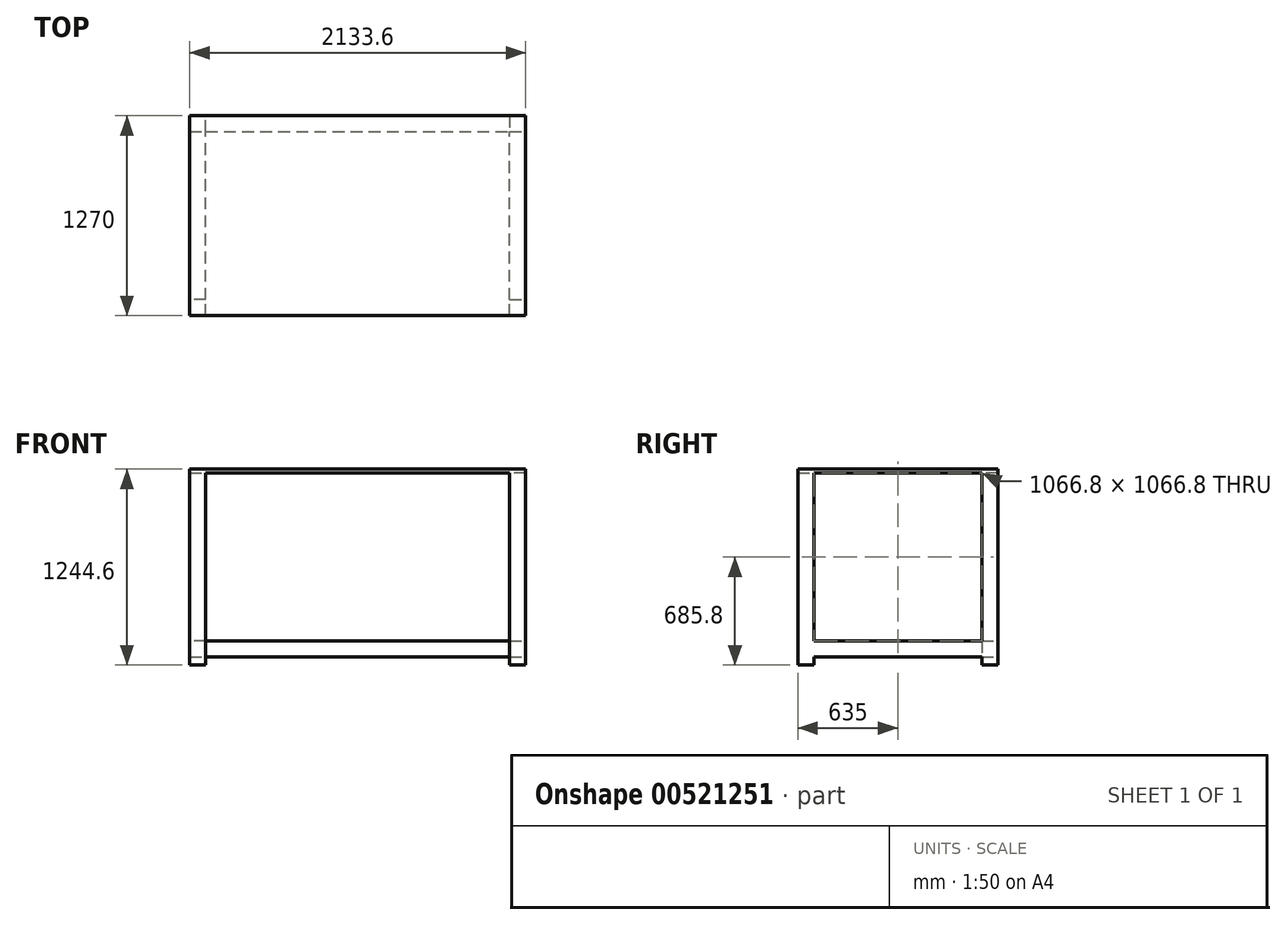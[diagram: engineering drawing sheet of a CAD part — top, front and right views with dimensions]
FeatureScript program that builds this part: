
annotation { "Feature Type Name" : "Feature", "Feature Type Description" : "" }
export const myFeature = defineFeature(function(context is Context, id is Id, definition is map)
    precondition{}
    {
        {
            var Q0;
            Q0=qCreatedBy(makeId("Top.planeOp"),FACE);
            var sketch = newSketch(context, id + "F0", { "sketchPlane" : qUnion([Q0])});
            skLineSegment(sketch, "E0.bottom", {"start": v(1066.8, -635) * mm, "end": v(-1066.8, -635) * mm, "construction": true});
            skLineSegment(sketch, "E0.top", {"start": v(1066.8, 635) * mm, "end": v(-1066.8, 635) * mm, "construction": true});
            skLineSegment(sketch, "E0.left", {"start": v(1066.8, -635) * mm, "end": v(1066.8, 635) * mm, "construction": true});
            skLineSegment(sketch, "E0.right", {"start": v(-1066.8, -635) * mm, "end": v(-1066.8, 635) * mm, "construction": true});
            skPoint(sketch, "E0.middle", {"position": v(0, 0) * mm});
            skLineSegment(sketch, "E1.bottom", {"start": v(-1066.8, 635) * mm, "end": v(-965.2, 635) * mm});
            skLineSegment(sketch, "E1.top", {"start": v(-1066.8, 533.4) * mm, "end": v(-965.2, 533.4) * mm});
            skLineSegment(sketch, "E1.left", {"start": v(-1066.8, 635) * mm, "end": v(-1066.8, 533.4) * mm});
            skLineSegment(sketch, "E1.right", {"start": v(-965.2, 635) * mm, "end": v(-965.2, 533.4) * mm});
            skLineSegment(sketch, "E2.bottom", {"start": v(-1066.8, -635) * mm, "end": v(-965.2, -635) * mm});
            skLineSegment(sketch, "E2.top", {"start": v(-1066.8, -533.4) * mm, "end": v(-965.2, -533.4) * mm});
            skLineSegment(sketch, "E2.left", {"start": v(-1066.8, -635) * mm, "end": v(-1066.8, -533.4) * mm});
            skLineSegment(sketch, "E2.right", {"start": v(-965.2, -635) * mm, "end": v(-965.2, -533.4) * mm});
            skLineSegment(sketch, "E3.bottom", {"start": v(1066.8, -635) * mm, "end": v(965.2, -635) * mm});
            skLineSegment(sketch, "E3.top", {"start": v(1066.8, -533.4) * mm, "end": v(965.2, -533.4) * mm});
            skLineSegment(sketch, "E3.left", {"start": v(1066.8, -635) * mm, "end": v(1066.8, -533.4) * mm});
            skLineSegment(sketch, "E3.right", {"start": v(965.2, -635) * mm, "end": v(965.2, -533.4) * mm});
            skLineSegment(sketch, "E4.bottom", {"start": v(1066.8, 635) * mm, "end": v(965.2, 635) * mm});
            skLineSegment(sketch, "E4.top", {"start": v(1066.8, 533.4) * mm, "end": v(965.2, 533.4) * mm});
            skLineSegment(sketch, "E4.left", {"start": v(1066.8, 635) * mm, "end": v(1066.8, 533.4) * mm});
            skLineSegment(sketch, "E4.right", {"start": v(965.2, 635) * mm, "end": v(965.2, 533.4) * mm});
            skSolve(sketch);
        }
        {
            var Q0;
            Q0 = qSketchRegion(id + "F0", true);
            extrude(context, id + "F1", {"entities" : qUnion([Q0]), "depth" : 1219.2 * mm, "offsetDistance" : 25.4 * mm});
        }
        {
            var Q0;
            Q0=makeQuery(id+"F1.opExtrude","CAP_FACE",FACE,{"disambiguationData":[OSD([sQuery(id+"F0.wireOp",EDGE,"E1.bottom"),sQuery(id+"F0.wireOp",EDGE,"E1.top"),sQuery(id+"F0.wireOp",EDGE,"E1.left"),sQuery(id+"F0.wireOp",EDGE,"E1.right")])],"isStart":false});
            var sketch = newSketch(context, id + "F2", { "sketchPlane" : qUnion([Q0])});
            skLineSegment(sketch, "E5.bottom", {"start": v(-1066.8, 635) * mm, "end": v(1066.8, 635) * mm});
            skLineSegment(sketch, "E5.top", {"start": v(-1066.8, -635) * mm, "end": v(1066.8, -635) * mm});
            skLineSegment(sketch, "E5.left", {"start": v(-1066.8, 635) * mm, "end": v(-1066.8, -635) * mm});
            skLineSegment(sketch, "E5.right", {"start": v(1066.8, 635) * mm, "end": v(1066.8, -635) * mm});
            skSolve(sketch);
        }
        {
            var Q0;
            Q0 = qSketchRegion(id + "F2", true);
            extrude(context, id + "F3", {"entities" : qUnion([Q0]), "operationType" : NewBodyOperationType.ADD, "depth" : 25.4 * mm, "offsetDistance" : 25.4 * mm});
        }
        {
            var Q0;
            Q0=makeQuery(id+"F1.opExtrude","SWEPT_FACE",FACE,{"disambiguationData":[OSD([sQuery(id+"F0.wireOp",EDGE,"E1.top")])]});
            var sketch = newSketch(context, id + "F4", { "sketchPlane" : qUnion([Q0])});
            skLineSegment(sketch, "E6", {"start": v(-1066.8, 0) * mm, "end": v(-1066.8, 50.8) * mm, "construction": true});
            skLineSegment(sketch, "E7.bottom", {"start": v(-1066.8, 50.8) * mm, "end": v(-965.2, 50.8) * mm});
            skLineSegment(sketch, "E7.top", {"start": v(-1066.8, 152.4) * mm, "end": v(-965.2, 152.4) * mm});
            skLineSegment(sketch, "E7.left", {"start": v(-1066.8, 50.8) * mm, "end": v(-1066.8, 152.4) * mm});
            skLineSegment(sketch, "E7.right", {"start": v(-965.2, 50.8) * mm, "end": v(-965.2, 152.4) * mm});
            skLineSegment(sketch, "E8.bottom", {"start": v(965.2, 50.8) * mm, "end": v(1066.8, 50.8) * mm});
            skLineSegment(sketch, "E8.top", {"start": v(965.2, 152.4) * mm, "end": v(1066.8, 152.4) * mm});
            skLineSegment(sketch, "E8.left", {"start": v(965.2, 50.8) * mm, "end": v(965.2, 152.4) * mm});
            skLineSegment(sketch, "E8.right", {"start": v(1066.8, 50.8) * mm, "end": v(1066.8, 152.4) * mm});
            skSolve(sketch);
        }
        {
            var Q0;
            Q0 = qSketchRegion(id + "F4", true);
            extrude(context, id + "F5", {"entities" : qUnion([Q0]), "operationType" : NewBodyOperationType.ADD, "endBound" : BoundingType.UP_TO_NEXT, "depth" : 25.4 * mm, "offsetDistance" : 25.4 * mm});
        }
        {
            var Q0;
            Q0=makeQuery(id+"F5.boolean.opBoolean","MERGE",FACE,{"derivedFrom":[makeQuery(id+"F1.opExtrude","SWEPT_FACE",FACE,{"disambiguationData":[OSD([sQuery(id+"F0.wireOp",EDGE,"E3.right")])]}),makeQuery(id+"F1.opExtrude","SWEPT_FACE",FACE,{"disambiguationData":[OSD([sQuery(id+"F0.wireOp",EDGE,"E4.right")])]}),makeQuery(id+"F5.opExtrude","SWEPT_FACE",FACE,{"disambiguationData":[OSD([sQuery(id+"F4.wireOp",EDGE,"E8.left")])]})]});
            var sketch = newSketch(context, id + "F6", { "sketchPlane" : qUnion([Q0])});
            skLineSegment(sketch, "E9", {"start": v(-635, 0) * mm, "end": v(-635, 50.8) * mm, "construction": true});
            skLineSegment(sketch, "E10.bottom", {"start": v(-635, 50.8) * mm, "end": v(-533.4, 50.8) * mm});
            skLineSegment(sketch, "E10.top", {"start": v(-635, 152.4) * mm, "end": v(-533.4, 152.4) * mm});
            skLineSegment(sketch, "E10.left", {"start": v(-635, 50.8) * mm, "end": v(-635, 152.4) * mm});
            skLineSegment(sketch, "E10.right", {"start": v(-533.4, 50.8) * mm, "end": v(-533.4, 152.4) * mm});
            skSolve(sketch);
        }
        {
            var Q0;
            Q0 = qSketchRegion(id + "F6", true);
            extrude(context, id + "F7", {"entities" : qUnion([Q0]), "operationType" : NewBodyOperationType.ADD, "endBound" : BoundingType.UP_TO_NEXT, "depth" : 25.4 * mm, "offsetDistance" : 25.4 * mm});
        }
    });
